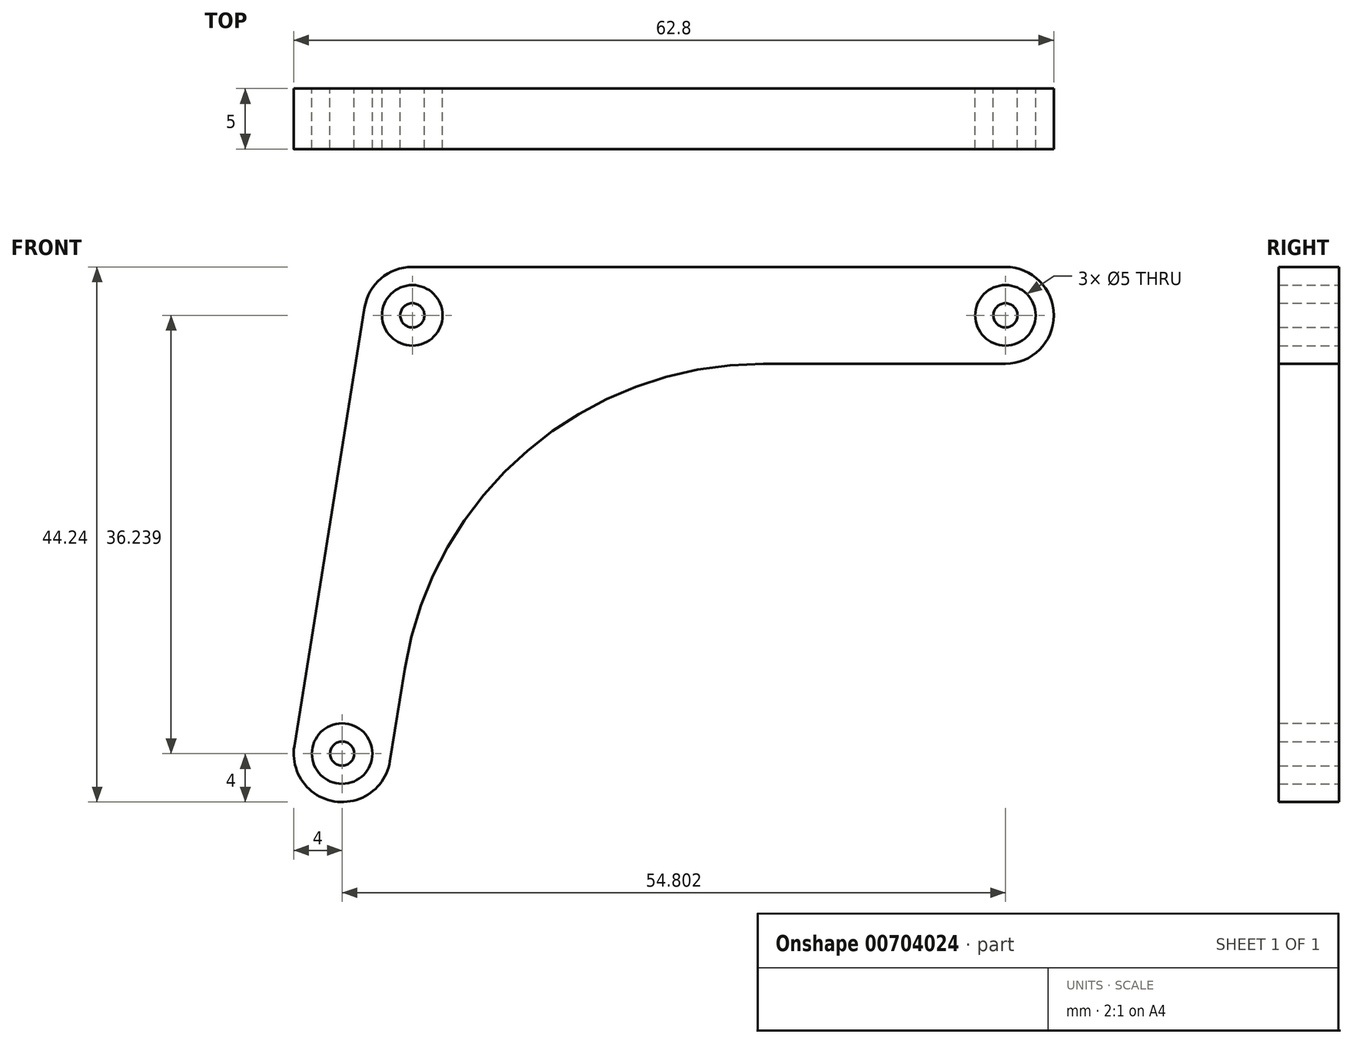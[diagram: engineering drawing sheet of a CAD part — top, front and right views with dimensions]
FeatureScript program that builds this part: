
annotation { "Feature Type Name" : "Feature", "Feature Type Description" : "" }
export const myFeature = defineFeature(function(context is Context, id is Id, definition is map)
    precondition{}
    {
        {
            var Q0;
            Q0=qCreatedBy(makeId("Front.planeOp"),FACE);
            var sketch = newSketch(context, id + "F0", { "sketchPlane" : qUnion([Q0])});
            skLineSegment(sketch, "E0", {"start": v(0, 0) * mm, "end": v(5.8, 36.24) * mm, "construction": true});
            skLineSegment(sketch, "E1", {"start": v(5.8, 36.24) * mm, "end": v(54.8, 36.24) * mm, "construction": true});
            skLineSegment(sketch, "E2", {"start": v(54.8, 36.24) * mm, "end": v(0, 0) * mm, "construction": true});
            skCircle(sketch, "E3", {"center": v(0, 0) * mm, "radius": 4 * mm});
            skCircle(sketch, "E4", {"center": v(0, 0) * mm, "radius": 2.5 * mm});
            skCircle(sketch, "E5", {"center": v(0, 0) * mm, "radius": 1 * mm});
            skCircle(sketch, "E6", {"center": v(5.8, 36.24) * mm, "radius": 4 * mm});
            skCircle(sketch, "E7", {"center": v(5.8, 36.24) * mm, "radius": 2.5 * mm});
            skCircle(sketch, "E8", {"center": v(5.8, 36.24) * mm, "radius": 1 * mm});
            skCircle(sketch, "E9", {"center": v(54.8, 36.24) * mm, "radius": 4 * mm});
            skCircle(sketch, "E10", {"center": v(54.8, 36.24) * mm, "radius": 2.5 * mm});
            skCircle(sketch, "E11", {"center": v(54.8, 36.24) * mm, "radius": 1 * mm});
            skLineSegment(sketch, "E12", {"start": v(54.8, 40.24) * mm, "end": v(5.8, 40.24) * mm});
            skLineSegment(sketch, "E13", {"start": v(1.85, 36.87) * mm, "end": v(-3.95, 0.63) * mm});
            skLineSegment(sketch, "E14", {"start": v(3.95, -0.63) * mm, "end": v(5.17, 6.98) * mm});
            skArc(sketch, "E15", {"start": v(34.8, 32.24) * mm, "mid": v(15.33, 25.07) * mm, "end": v(5.17, 6.98) * mm});
            skLineSegment(sketch, "E16.trimOffspring", {"start": v(34.8, 32.24) * mm, "end": v(54.8, 32.24) * mm});
            skSolve(sketch);
        }
        {
            var Q0;
            Q0 = qSketchRegion(id + "F0", true);
            var Q1;
            Q1=makeQuery(id+"F0.imprint","IMPRINT",FACE,{"disambiguationData":[TD([[makeQuery(id+"F0.imprint","IMPRINT",EDGE,{"derivedFrom":sQuery(id+"F0.wireOp",EDGE,"E8")}),1.0]])]});
            var Q2;
            Q2=makeQuery(id+"F0.imprint","IMPRINT",FACE,{"disambiguationData":[TD([[makeQuery(id+"F0.imprint","IMPRINT",EDGE,{"derivedFrom":sQuery(id+"F0.wireOp",EDGE,"E5")}),1.0]])]});
            var Q3;
            Q3=makeQuery(id+"F0.imprint","IMPRINT",FACE,{"disambiguationData":[TD([[makeQuery(id+"F0.imprint","IMPRINT",EDGE,{"derivedFrom":sQuery(id+"F0.wireOp",EDGE,"E11")}),1.0]])]});
            extrude(context, id + "F1", {"entities" : qUnion([Q0, Q1, Q2, Q3]), "depth" : 5 * mm, "offsetDistance" : 25 * mm});
        }
    });
